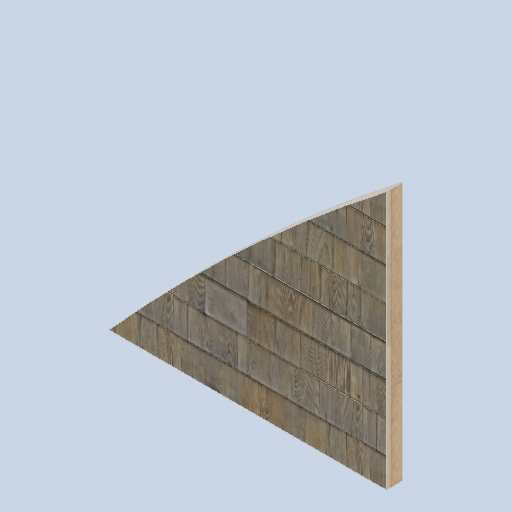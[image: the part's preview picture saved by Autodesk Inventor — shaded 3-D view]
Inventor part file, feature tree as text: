
AUTODESK INVENTOR PART (.ipt)
format: ipt  version: 2024.2 (Build 282272000, 272)  size: 367,616 bytes
history: native  units: mm
features: extrude x1, sketch x1
ambient origin geometry x8: Origin, YZ Plane, XZ Plane, XY Plane, X Axis, Y Axis, Z Axis, Center Point
bodies: Solid1 (feature_tree)
feature tree (2):
  extrude  "Extrusion1"  [1 undecoded]
  sketch  "Sketch1"  dims[d0=80.0mm d1=0.0mm]
note: 1 required parameter value undecoded (feature->parameter linkage not recoverable at this tier; creation-order binding heuristic only, values carry confidence <= 0.55)
